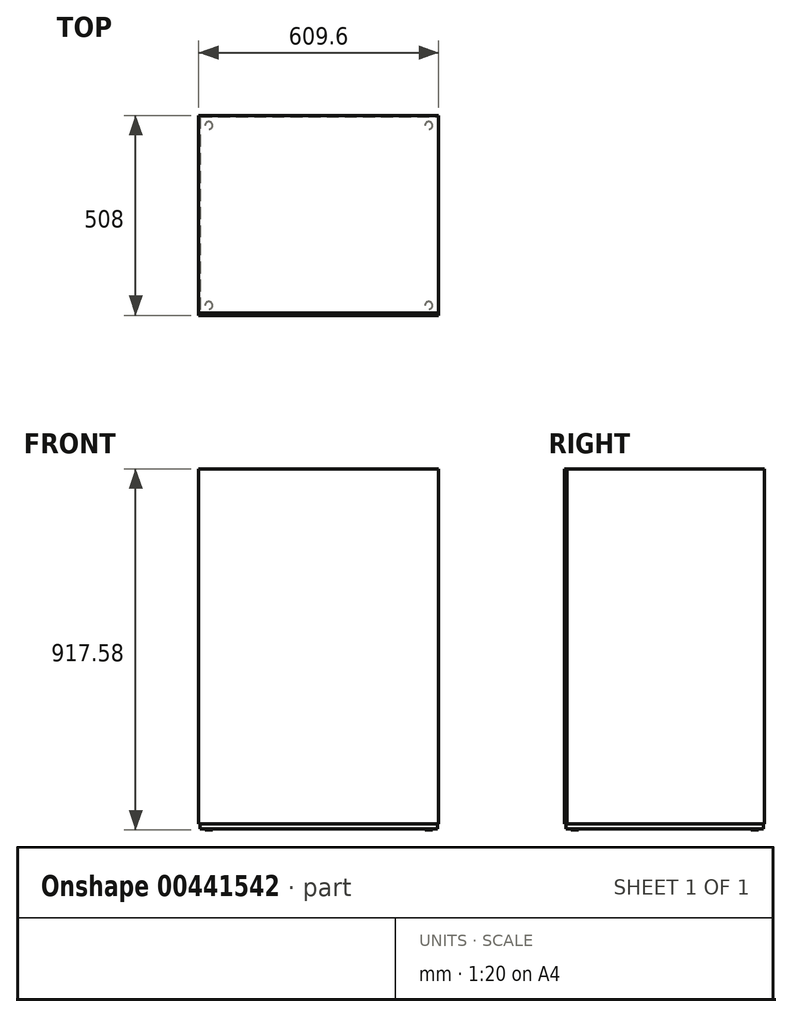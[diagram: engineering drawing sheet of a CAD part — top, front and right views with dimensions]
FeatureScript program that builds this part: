
annotation { "Feature Type Name" : "Feature", "Feature Type Description" : "" }
export const myFeature = defineFeature(function(context is Context, id is Id, definition is map)
    precondition{}
    {
        {
            var Q0;
            Q0=qCreatedBy(makeId("Top.planeOp"),FACE);
            var sketch = newSketch(context, id + "F0", { "sketchPlane" : qUnion([Q0])});
            skLineSegment(sketch, "E0.bottom", {"start": v(-301.62, 250.83) * mm, "end": v(301.62, 250.83) * mm});
            skLineSegment(sketch, "E0.top", {"start": v(-301.63, -250.83) * mm, "end": v(301.63, -250.83) * mm});
            skLineSegment(sketch, "E0.left", {"start": v(-301.63, 250.83) * mm, "end": v(-301.63, -250.83) * mm});
            skLineSegment(sketch, "E0.right", {"start": v(301.63, 250.83) * mm, "end": v(301.63, -250.83) * mm});
            skLineSegment(sketch, "E1", {"start": v(0, 250.82) * mm, "end": v(0, -250.82) * mm, "construction": true});
            skLineSegment(sketch, "E2", {"start": v(-301.63, 0) * mm, "end": v(301.63, 0) * mm, "construction": true});
            skPoint(sketch, "E3", {"position": v(0, 0) * mm});
            skSolve(sketch);
        }
        {
            var Q0;
            Q0=qSketchRegion(id+"F0",true);
            extrude(context, id + "F1", {"entities" : qUnion([Q0]), "depth" : 12.7 * mm});
        }
        {
            var Q0;
            Q0=makeQuery(id+"F1.opExtrude","CAP_FACE",FACE,{"disambiguationData":[OSD([sQuery(id+"F0.wireOp",EDGE,"E0.bottom"),sQuery(id+"F0.wireOp",EDGE,"E0.top"),sQuery(id+"F0.wireOp",EDGE,"E0.left"),sQuery(id+"F0.wireOp",EDGE,"E0.right")])],"isStart":false});
            var sketch = newSketch(context, id + "F2", { "sketchPlane" : qUnion([Q0])});
            skLineSegment(sketch, "E4.0", {"start": v(-304.8, 254) * mm, "end": v(-304.8, -254) * mm});
            skLineSegment(sketch, "E4.1", {"start": v(-304.8, 254) * mm, "end": v(304.8, 254) * mm});
            skLineSegment(sketch, "E4.2", {"start": v(304.8, 254) * mm, "end": v(304.8, -254) * mm});
            skLineSegment(sketch, "E4.3", {"start": v(-304.8, -254) * mm, "end": v(304.8, -254) * mm});
            skLineSegment(sketch, "E5", {"start": v(-304.8, -247.65) * mm, "end": v(304.8, -247.65) * mm});
            skSolve(sketch);
        }
        {
            var Q0;
            {var subQ5=makeQuery(id+"F1.opExtrude","CAP_EDGE",EDGE,{"disambiguationData":[OSD([sQuery(id+"F0.wireOp",EDGE,"E0.bottom")])],"isStart":false});Q0=makeQuery(id+"F2.imprint","IMPRINT",FACE,{"disambiguationData":[TD([[makeQuery(id+"F2.imprint","IMPRINT",EDGE,{"derivedFrom":subQ5}),-1.0]])]});}
            var Q1;
            {var subQ6=sQuery(id+"F2.wireOp",EDGE,"E4.1");Q1=makeQuery(id+"F2.imprint","IMPRINT",FACE,{"disambiguationData":[TD([[makeQuery(id+"F2.imprint","IMPRINT",EDGE,{"derivedFrom":subQ6}),-1.0]])]});}
            extrude(context, id + "F3", {"entities" : qUnion([Q0, Q1]), "operationType" : NewBodyOperationType.ADD, "depth" : 901.7 * mm, "offsetDistance" : 25.4 * mm});
        }
        {
            var Q0;
            {var subQ5=makeQuery(id+"F1.opExtrude","CAP_EDGE",EDGE,{"disambiguationData":[OSD([sQuery(id+"F0.wireOp",EDGE,"E0.top")])],"isStart":false});Q0=makeQuery(id+"F2.imprint","IMPRINT",FACE,{"disambiguationData":[TD([[makeQuery(id+"F2.imprint","IMPRINT",EDGE,{"derivedFrom":subQ5}),1.0]])]});}
            var Q1;
            {var subQ0=sQuery(id+"F2.wireOp",EDGE,"E4.3");Q1=makeQuery(id+"F2.imprint","IMPRINT",FACE,{"disambiguationData":[TD([[makeQuery(id+"F2.imprint","IMPRINT",EDGE,{"derivedFrom":subQ0}),1.0]])]});}
            extrude(context, id + "F4", {"entities" : qUnion([Q0, Q1]), "depth" : 901.7 * mm, "offsetDistance" : 25.4 * mm});
        }
        {
            var Q0;
            Q0=makeQuery(id+"F1.opExtrude","CAP_FACE",FACE,{"disambiguationData":[OSD([sQuery(id+"F0.wireOp",EDGE,"E0.bottom"),sQuery(id+"F0.wireOp",EDGE,"E0.top"),sQuery(id+"F0.wireOp",EDGE,"E0.left"),sQuery(id+"F0.wireOp",EDGE,"E0.right")])],"isStart":true});
            var sketch = newSketch(context, id + "F5", { "sketchPlane" : qUnion([Q0])});
            skPoint(sketch, "E6", {"position": v(0, 0) * mm});
            skCircle(sketch, "E7", {"center": v(-279.4, 228.6) * mm, "radius": 9.53 * mm});
            skCircle(sketch, "E8.0.1.0", {"center": v(-279.4, -228.6) * mm, "radius": 9.53 * mm});
            skCircle(sketch, "E8.1.0.0", {"center": v(279.4, 228.6) * mm, "radius": 9.53 * mm});
            skCircle(sketch, "E8.1.1.0", {"center": v(279.4, -228.6) * mm, "radius": 9.53 * mm});
            skLineSegment(sketch, "E8.direction1", {"start": v(-279.4, 228.6) * mm, "end": v(279.4, 228.6) * mm, "construction": true});
            skLineSegment(sketch, "E8.direction2", {"start": v(-279.4, 228.6) * mm, "end": v(-279.4, -228.6) * mm, "construction": true});
            skSolve(sketch);
        }
        {
            var Q0;
            Q0=qSketchRegion(id+"F5",true);
            extrude(context, id + "F6", {"entities" : qUnion([Q0]), "depth" : 3.17 * mm});
        }
    });
